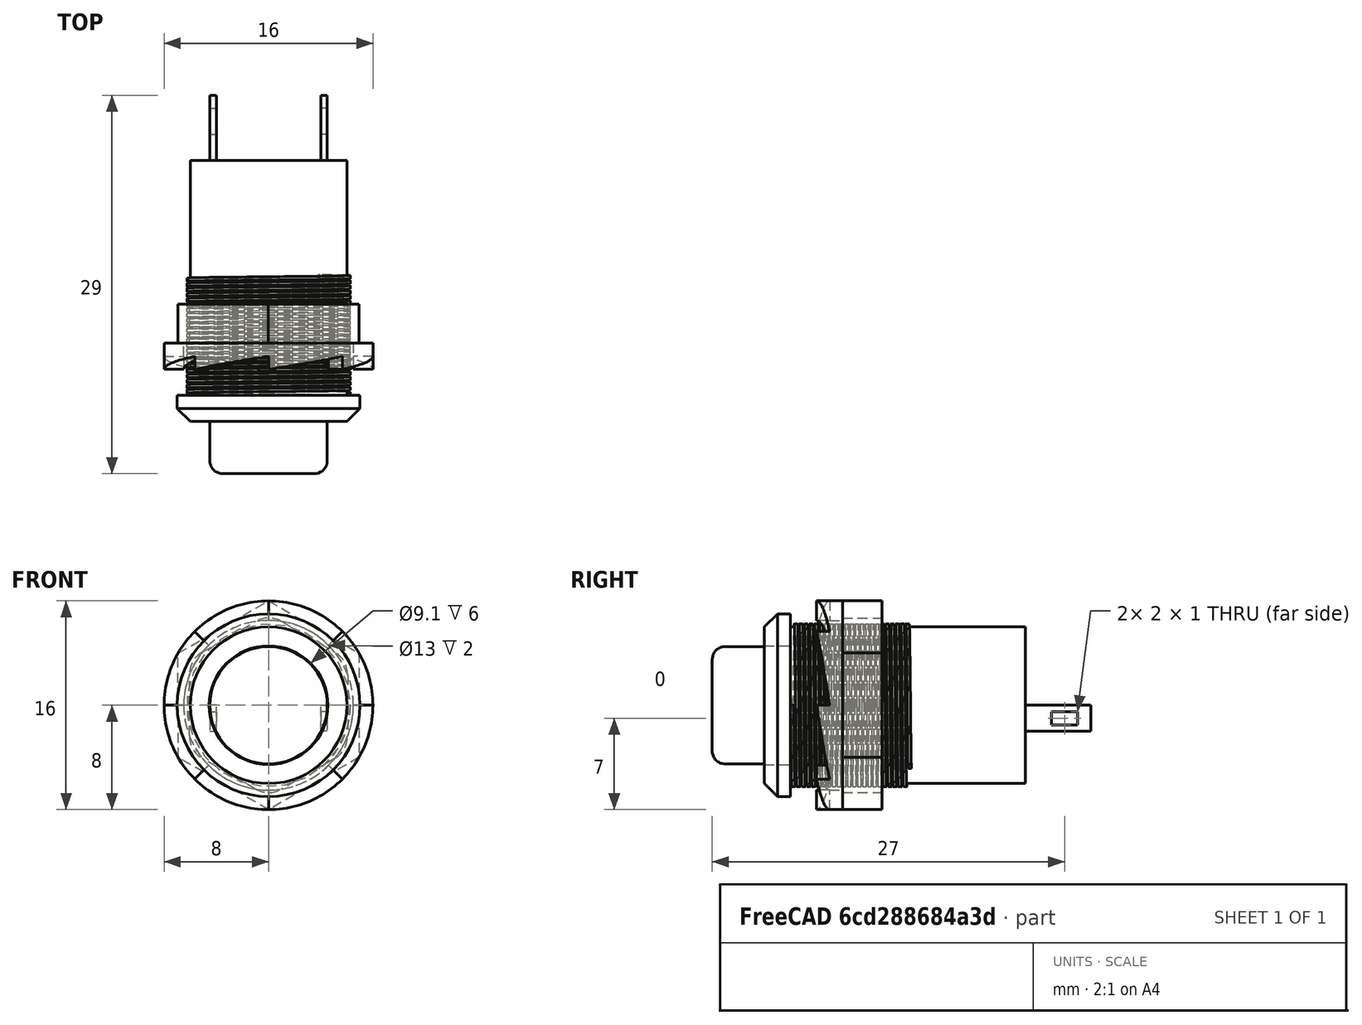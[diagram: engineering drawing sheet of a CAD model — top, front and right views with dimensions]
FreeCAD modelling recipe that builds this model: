
FCSTD DOCUMENT  (FreeCAD 1.1R20260414 (Git shallow))
Label: spring_button
License: All rights reserved
LicenseURL: https://en.wikipedia.org/wiki/All_rights_reserved
objects: Sketcher::SketchObject×9, PartDesign::Pad×6, App::Point×5, PartDesign::Body×4, App::Link×4, App::FeaturePython×4, PartDesign::ShapeBinder×2, PartDesign::Plane×2, PartDesign::Fillet×2, PartDesign::Chamfer×1, PartDesign::Hole×1, PartDesign::AdditiveHelix×1, PartDesign::Pocket×1, PartDesign::Mirrored×1, PartDesign::SubtractiveHelix×1, PartDesign::PolarPattern×1, Assembly::JointGroup×1, Assembly::AssemblyObject×1
note: 69 computed .brp shape members not serialized (recipe doc carries the construction recipe); baked Part::Feature solids carry a one-line shape summary decoded from their .brp

FEATURE [App::Point] Origin001
  Role = Origin
FEATURE [Sketcher::SketchObject] Sketch
  ArcFitTolerance = 1e-06
  AttachmentSupport = -> [Origin]
  ExternalTypes = [0]
  FullyConstrained = true
  MakeInternals = false
  MapMode = 5
  Placement = pos=(0,0,0) rot=(1,0,0;1.5708rad)
  _ExternalGeoVersion = 1
  sketch-geometry (1):
    g0: Circle CenterX=0 CenterY=0 CenterZ=0 NormalX=0 NormalY=0 NormalZ=1 AngleXU=0 Radius=6
  constraints (2):
    c: Diameter(g0) = 12
    c: Coincident(g0,g-1)
FEATURE [PartDesign::Pad] Pad
  Direction = (0,-1,2e-16)
  Length = 18
  Length2 = 10
  Profile = -> Sketch
  ReferenceAxis = -> Sketch [N_Axis]
  Refine = true
  SideType = 0
  Suppressed = false
  Type = 0
  Type2 = 0
FEATURE [Sketcher::SketchObject] Sketch001
  ArcFitTolerance = 1e-06
  AttachmentSupport = -> [Pad]
  ExternalTypes = [0]
  FullyConstrained = true
  MakeInternals = false
  MapMode = 5
  Placement = pos=(0,-18,0) rot=(1,0,0;1.5708rad)
  _ExternalGeoVersion = 1
  sketch-geometry (1):
    g0: Circle CenterX=0 CenterY=0 CenterZ=0 NormalX=0 NormalY=0 NormalZ=1 AngleXU=0 Radius=7
  constraints (2):
    c: Diameter(g0) = 14
    c: Coincident(g0,g-1)
FEATURE [PartDesign::Pad] Pad001
  BaseFeature = -> Pad
  Direction = (0,-1,2e-16)
  Length = 2
  Length2 = 10
  Profile = -> Sketch001
  ReferenceAxis = -> Sketch001 [N_Axis]
  Refine = true
  SideType = 0
  Suppressed = false
  Type = 0
  Type2 = 0
FEATURE [PartDesign::Chamfer] Chamfer
  Angle = 45
  Base = -> Pad001 [Edge6]
  BaseFeature = -> Pad001
  ChamferType = 0
  FlipDirection = false
  Refine = true
  Size = 1
  Size2 = 1
  SupportTransform = false
  Suppressed = false
  UseAllEdges = false
FEATURE [PartDesign::Hole] Hole
  BaseFeature = -> Chamfer
  BaseProfileType = 7
  CustomThreadClearance = 0
  Depth = 6
  DepthType = 0
  Diameter = 9.1
  DrillForDepth = false
  DrillPoint = 0
  DrillPointAngle = 118
  HoleCutCountersinkAngle = 90
  HoleCutCustomValues = false
  HoleCutDepth = 0
  HoleCutDiameter = 0
  HoleCutType = 0
  ModelThread = false
  Profile = -> Chamfer [Face4]
  Refine = true
  Suppressed = false
  Tapered = false
  TaperedAngle = 90
  ThreadClass = 0
  ThreadDepth = 6
  ThreadDepthType = 0
  ThreadDiameter = 9.1
  ThreadDirection = 0
  ThreadFit = 0
  ThreadSize = 0
  ThreadType = 0
  Threaded = false
  UseCustomThreadClearance = false
FEATURE [Sketcher::SketchObject] Sketch004
  ArcFitTolerance = 1e-06
  AttachmentSupport = -> [Origin]
  ExternalTypes = [0]
  FullyConstrained = true
  MakeInternals = false
  MapMode = 5
  _ExternalGeoVersion = 1
  sketch-geometry (4):
    g0: LineSegment StartX=6 StartY=-18 StartZ=0 EndX=6.25 EndY=-18 EndZ=0
    g1: LineSegment StartX=6.25 StartY=-18 StartZ=0 EndX=6.25 EndY=-17.75 EndZ=0
    g2: LineSegment StartX=6.25 StartY=-17.75 StartZ=0 EndX=6 EndY=-17.75 EndZ=0
    g3: LineSegment StartX=6 StartY=-17.75 StartZ=0 EndX=6 EndY=-18 EndZ=0
  constraints (11):
    c: Coincident(g0,g-3)
    c: Horizontal(g0)
    c: Coincident(g1,g0)
    c: Vertical(g1)
    c: Coincident(g2,g1)
    c: PointOnObject(g2,g-3)
    c: Horizontal(g2)
    c: DistanceY(g1,g1) = 0.25
    c: DistanceX(g2,g2) = 0.25
    c: Coincident(g3,g2)
    c: Coincident(g3,g0)
FEATURE [PartDesign::AdditiveHelix] AdditiveHelix
  Angle = 0
  Axis = (0,1,0)
  Base = (0,0,0)
  BaseFeature = -> Hole
  Growth = 0
  HasBeenEdited = true
  Height = 9
  LeftHanded = false
  Mode = 0
  Outside = false
  Pitch = 0.388909
  Profile = -> Sketch004
  ReferenceAxis = -> Sketch004 [V_Axis]
  Refine = true
  Suppressed = false
  Tolerance = 0.1
  Turns = 23.1417
FEATURE [PartDesign::Body] Body  label="base"
  AllowCompound = true
  Group = -> [Sketch,Pad,Sketch001,Pad001,Chamfer,Hole,Sketch004,AdditiveHelix]
  Origin = -> Origin
  Tip = -> AdditiveHelix
FEATURE [App::Point] Origin003
  Role = Origin
FEATURE [PartDesign::ShapeBinder] CopyAdditiveHelix
  TraceSupport = false
FEATURE [PartDesign::Plane] DatumPlane
  AttachmentSupport = -> [CopyAdditiveHelix]
  Length = 60
  MapMode = 5
  Placement = pos=(0,0,0) rot=(0,0.707107,0.707107;3.14159rad)
  ResizeMode = 0
  Width = 60
FEATURE [Sketcher::SketchObject] Sketch005
  ArcFitTolerance = 1e-06
  AttachmentSupport = -> [DatumPlane]
  ExternalGeometry = -> [CopyAdditiveHelix]
  ExternalTypes = [0]
  FullyConstrained = true
  MakeInternals = false
  MapMode = 5
  Placement = pos=(0,0,0) rot=(0,0.707107,0.707107;3.14159rad)
  _ExternalGeoVersion = 1
  sketch-geometry (4):
    g0: LineSegment StartX=4 StartY=0 StartZ=0 EndX=4.5 EndY=0 EndZ=0
    g1: LineSegment StartX=4.5 StartY=0 StartZ=0 EndX=4.5 EndY=-2 EndZ=0
    g2: LineSegment StartX=4.5 StartY=-2 StartZ=0 EndX=4 EndY=-2 EndZ=0
    g3: LineSegment StartX=4 StartY=-2 StartZ=0 EndX=4 EndY=0 EndZ=0
  constraints (12):
    c: Coincident(g0,g1)
    c: Coincident(g1,g2)
    c: Coincident(g2,g3)
    c: Coincident(g3,g0)
    c: Horizontal(g0)
    c: Horizontal(g2)
    c: Vertical(g1)
    c: Vertical(g3)
    c: Distance(g1,g3) = 0.5
    c: Distance(g0,g2) = 2
    c: PointOnObject(g0,g-1)
    c: Distance(g-3,g3) = 2
FEATURE [PartDesign::Pad] Pad002
  Direction = (0,1,-2e-16)
  Length = 5
  Length2 = 10
  Placement = pos=(0,0,0) rot=(0,0.707107,0.707107;3.14159rad)
  Profile = -> Sketch005
  ReferenceAxis = -> Sketch005 [N_Axis]
  Refine = true
  SideType = 0
  Suppressed = false
  Type = 0
  Type2 = 0
FEATURE [Sketcher::SketchObject] Sketch006
  ArcFitTolerance = 1e-06
  AttachmentSupport = -> [Pad002]
  ExternalTypes = [0]
  FullyConstrained = true
  MakeInternals = false
  MapMode = 5
  Placement = pos=(-4.5,-4e-16,4e-16) rot=(0,-1,0;1.5708rad)
  _ExternalGeoVersion = 1
  sketch-geometry (4):
    g0: LineSegment StartX=-1.5 StartY=4 StartZ=0 EndX=-1.5 EndY=2 EndZ=0
    g1: LineSegment StartX=-1.5 StartY=2 StartZ=0 EndX=-0.5 EndY=2 EndZ=0
    g2: LineSegment StartX=-0.5 StartY=2 StartZ=0 EndX=-0.5 EndY=4 EndZ=0
    g3: LineSegment StartX=-0.5 StartY=4 StartZ=0 EndX=-1.5 EndY=4 EndZ=0
  constraints (12):
    c: Coincident(g0,g1)
    c: Coincident(g1,g2)
    c: Coincident(g2,g3)
    c: Coincident(g3,g0)
    c: Vertical(g0)
    c: Vertical(g2)
    c: Horizontal(g1)
    c: Horizontal(g3)
    c: DistanceY(g2,g2) = 2
    c: DistanceX(g3,g3) = 1
    c: Distance(g-2,g2) = 0.5
    c: Distance(g-1,g1) = 2
FEATURE [PartDesign::Pocket] Pocket
  BaseFeature = -> Pad002
  Direction = (1,0,-2e-16)
  Length = 5
  Length2 = 5
  Placement = pos=(0,0,0) rot=(0,0.707107,0.707107;3.14159rad)
  Profile = -> Sketch006
  ReferenceAxis = -> Sketch006 [N_Axis]
  Refine = true
  SideType = 0
  Suppressed = false
  Type = 1
  Type2 = 0
FEATURE [PartDesign::Mirrored] Mirrored
  BaseFeature = -> Pocket
  MirrorPlane = -> YZ_Plane001
  Originals = -> [Pad002,Pocket]
  Placement = pos=(0,0,0) rot=(0,0.707107,0.707107;3.14159rad)
  Refine = true
  Suppressed = false
  TransformMode = 0
FEATURE [PartDesign::Body] Body001  label="pins"
  AllowCompound = true
  Group = -> [DatumPlane,CopyAdditiveHelix,Sketch005,Pad002,Sketch006,Pocket,Mirrored]
  Origin = -> Origin002
  Tip = -> Mirrored
FEATURE [App::Point] Origin005  label="Origin006"
  Role = Origin
FEATURE [PartDesign::ShapeBinder] CopyAdditiveHelix001
  Placement = pos=(0,-20,0) rot=(0,0,1;0rad)
  TraceSupport = false
FEATURE [PartDesign::Plane] DatumPlane001
  AttachmentSupport = -> [CopyAdditiveHelix001]
  Length = 60
  MapMode = 11
  Placement = pos=(0,-20,0) rot=(0.57735,0.57735,-0.57735;2.0944rad)
  ResizeMode = 0
  Width = 60
FEATURE [Sketcher::SketchObject] Sketch007
  ArcFitTolerance = 1e-06
  AttachmentSupport = -> [DatumPlane001]
  ExternalTypes = [0]
  FullyConstrained = true
  MakeInternals = false
  MapMode = 5
  Placement = pos=(0,-20,0) rot=(0.57735,0.57735,-0.57735;2.0944rad)
  _ExternalGeoVersion = 1
  sketch-geometry (1):
    g0: Circle CenterX=0 CenterY=0 CenterZ=0 NormalX=0 NormalY=0 NormalZ=1 AngleXU=0 Radius=4.5
  constraints (2):
    c: Diameter(g0) = 9
    c: Coincident(g0,g-1)
FEATURE [PartDesign::Pad] Pad003
  Direction = (0,-1,0)
  Length = 4
  Length2 = 10
  Placement = pos=(0,-20,0) rot=(0.57735,0.57735,-0.57735;2.0944rad)
  Profile = -> Sketch007
  ReferenceAxis = -> Sketch007 [N_Axis]
  Refine = true
  SideType = 0
  Suppressed = false
  Type = 0
  Type2 = 0
FEATURE [PartDesign::Fillet] Fillet
  Base = -> Pad003 [Edge3]
  BaseFeature = -> Pad003
  Placement = pos=(0,-20,0) rot=(0.57735,0.57735,-0.57735;2.0944rad)
  Radius = 1
  Refine = true
  SupportTransform = false
  Suppressed = false
  UseAllEdges = false
FEATURE [PartDesign::Body] Body002  label="button"
  AllowCompound = true
  Group = -> [DatumPlane001,CopyAdditiveHelix001,Sketch007,Pad003,Fillet]
  Origin = -> Origin004
  Tip = -> Fillet
FEATURE [App::Point] Origin007  label="Origin009"
  Role = Origin
FEATURE [Sketcher::SketchObject] Sketch008
  ArcFitTolerance = 1e-06
  AttachmentSupport = -> [Origin006]
  ExternalTypes = [0]
  FullyConstrained = true
  MakeInternals = false
  MapMode = 5
  Placement = pos=(0,0,0) rot=(1,0,0;1.5708rad)
  _ExternalGeoVersion = 1
  sketch-geometry (2):
    g0: Circle CenterX=0 CenterY=0 CenterZ=0 NormalX=0 NormalY=0 NormalZ=1 AngleXU=0 Radius=8
    g1: Circle CenterX=0 CenterY=0 CenterZ=0 NormalX=0 NormalY=0 NormalZ=1 AngleXU=0 Radius=6.5
  constraints (4):
    c: Diameter(g0) = 16
    c: Coincident(g0,g-1)
    c: Diameter(g1) = 13
    c: Coincident(g1,g0)
FEATURE [PartDesign::Pad] Pad004
  Direction = (0,-1,2e-16)
  Length = 2
  Length2 = 10
  Profile = -> Sketch008
  ReferenceAxis = -> Sketch008 [N_Axis]
  Refine = true
  SideType = 0
  Suppressed = false
  Type = 0
  Type2 = 0
FEATURE [Sketcher::SketchObject] Sketch009
  ArcFitTolerance = 1e-06
  AttachmentSupport = -> [Origin006]
  ExternalGeometry = -> [Pad004]
  ExternalTypes = [0,0]
  FullyConstrained = true
  MakeInternals = false
  MapMode = 5
  _ExternalGeoVersion = 1
  sketch-geometry (4):
    g0: LineSegment StartX=6.5 StartY=-2 StartZ=0 EndX=8 EndY=-2 EndZ=0
    g1: LineSegment StartX=8 StartY=-2 StartZ=0 EndX=8 EndY=-1 EndZ=0
    g2: LineSegment StartX=8 StartY=-1 StartZ=0 EndX=6.5 EndY=-1 EndZ=0
    g3: LineSegment StartX=6.5 StartY=-1 StartZ=0 EndX=6.5 EndY=-2 EndZ=0
  constraints (11):
    c: Coincident(g0,g1)
    c: Coincident(g1,g2)
    c: Coincident(g2,g3)
    c: Coincident(g3,g0)
    c: Horizontal(g0)
    c: Horizontal(g2)
    c: Vertical(g1)
    c: Vertical(g3)
    c: Coincident(g0,g-4)
    c: PointOnObject(g1,g-3)
    c: DistanceY(g1,g1) = 1
FEATURE [PartDesign::SubtractiveHelix] SubtractiveHelix
  Angle = 0
  Axis = (0,1,0)
  Base = (0,0,0)
  BaseFeature = -> Pad004
  Growth = 0
  HasBeenEdited = true
  Height = 1
  LeftHanded = false
  Mode = 0
  Outside = false
  Pitch = 8
  Profile = -> Sketch009
  ReferenceAxis = -> Sketch009 [V_Axis]
  Refine = true
  Reversed = true
  Suppressed = false
  Tolerance = 0.1
  Turns = 0.125
FEATURE [PartDesign::PolarPattern] PolarPattern
  Angle = 360
  Axis = -> Y_Axis003
  BaseFeature = -> SubtractiveHelix
  Mode = 0
  Occurrences = 8
  Offset = 120
  Originals = -> [SubtractiveHelix]
  Refine = true
  SpacingPattern = [0]
  Spacings = [-1,-1,-1,-1,-1,-1,-1]
  Suppressed = false
  TransformMode = 0
FEATURE [Sketcher::SketchObject] Sketch010
  ArcFitTolerance = 1e-06
  AttachmentSupport = -> [PolarPattern]
  ExternalGeometry = -> [PolarPattern]
  ExternalTypes = [0]
  FullyConstrained = false
  MakeInternals = false
  MapMode = 5
  Placement = pos=(0,0,0) rot=(0,0.707107,0.707107;3.14159rad)
  _ExternalGeoVersion = 1
  sketch-geometry (14):
    g0: LineSegment StartX=0.0147037 StartY=7.99999 StartZ=0 EndX=-6.92084 EndY=4.01273 EndZ=0
    g1: LineSegment StartX=-6.92084 StartY=4.01273 StartZ=0 EndX=-6.93554 EndY=-3.98726 EndZ=0
    g2: LineSegment StartX=-6.93554 StartY=-3.98726 StartZ=0 EndX=-0.0147037 EndY=-7.99999 EndZ=0
    g3: LineSegment StartX=-0.0147037 StartY=-7.99999 StartZ=0 EndX=6.92084 EndY=-4.01273 EndZ=0
    g4: LineSegment StartX=6.92084 StartY=-4.01273 StartZ=0 EndX=6.93554 EndY=3.98726 EndZ=0
    g5: LineSegment StartX=6.93554 StartY=3.98726 StartZ=0 EndX=0.0147037 EndY=7.99999 EndZ=0
    g6: Circle [constr] CenterX=0 CenterY=0 CenterZ=0 NormalX=0 NormalY=0 NormalZ=1 AngleXU=0 Radius=8
    g7: LineSegment StartX=0 StartY=6.99999 StartZ=0 EndX=-6.06217 EndY=3.49999 EndZ=0
    g8: LineSegment StartX=-6.06217 StartY=3.49999 StartZ=0 EndX=-6.06217 EndY=-3.49999 EndZ=0
    g9: LineSegment StartX=-6.06217 StartY=-3.49999 StartZ=0 EndX=9e-16 EndY=-6.99999 EndZ=0
    g10: LineSegment StartX=9e-16 StartY=-6.99999 StartZ=0 EndX=6.06217 EndY=-3.49999 EndZ=0
    g11: LineSegment StartX=6.06217 StartY=-3.49999 StartZ=0 EndX=6.06217 EndY=3.49999 EndZ=0
    g12: LineSegment StartX=6.06217 StartY=3.49999 StartZ=0 EndX=0 EndY=6.99999 EndZ=0
    g13: Circle [constr] CenterX=0 CenterY=0 CenterZ=0 NormalX=0 NormalY=0 NormalZ=1 AngleXU=0 Radius=6.99999
  constraints (31):
    c: Coincident(g0,g1)
    c: Coincident(g1,g2)
    c: Coincident(g2,g3)
    c: Coincident(g3,g4)
    c: Coincident(g4,g5)
    c: Coincident(g5,g0)
    c: Equal(g0, g1-g5) x5
    c: PointOnObject(g0,g6)
    c: PointOnObject(g1,g6)
    c: PointOnObject(g2,g6)
    c: PointOnObject(g3,g6)
    c: PointOnObject(g4,g6)
    c: PointOnObject(g5,g6)
    c: Coincident(g6,g-3)
    c: PointOnObject(g5,g-3)
    c: Coincident(g7,g8)
    c: Coincident(g8,g9)
    c: Coincident(g9,g10)
    c: Coincident(g10,g11)
    c: Coincident(g11,g12)
    c: Coincident(g12,g7)
    c: Equal(g7, g8-g12) x5
    c: PointOnObject(g7,g13)
    c: PointOnObject(g8,g13)
    c: PointOnObject(g9,g13)
    c: PointOnObject(g10,g13)
    c: PointOnObject(g11,g13)
    c: PointOnObject(g12,g13)
    c: Coincident(g13,g6)
    c: PointOnObject(g12,g-2)
    c: DistanceY(g7,g0) = 1
FEATURE [PartDesign::Pad] Pad005
  BaseFeature = -> PolarPattern
  Direction = (0,1,-2e-16)
  Length = 3
  Length2 = 10
  Profile = -> Sketch010
  ReferenceAxis = -> Sketch010 [N_Axis]
  Refine = true
  SideType = 0
  Suppressed = false
  Type = 0
  Type2 = 0
FEATURE [PartDesign::Fillet] Fillet001
  Base = -> Pad005 [Edge113,Edge118,Edge117,Edge114,Edge116,Edge115]
  BaseFeature = -> Pad005
  Radius = 2
  Refine = true
  SupportTransform = false
  Suppressed = false
  UseAllEdges = false
FEATURE [PartDesign::Body] Body003  label="nut"
  AllowCompound = true
  Group = -> [Sketch008,Pad004,Sketch009,SubtractiveHelix,PolarPattern,Sketch010,Pad005,Fillet001]
  Origin = -> Origin006
  Placement = pos=(0,-14,0) rot=(0,0,1;0rad)
  Tip = -> Fillet001
FEATURE [App::Point] Origin009  label="Origin011"
  Role = Origin
FEATURE [App::Link] base  label="base001"
  LinkedObject = -> Body
FEATURE [App::FeaturePython] GroundedJoint  # Assembly grounded joint (typed FeaturePython)
  ObjectToGround = -> base
FEATURE [App::Link] pins  label="pins001"
  LinkPlacement = pos=(-0.25,7e-16,1) rot=(0,0,1;0rad)
  LinkedObject = -> Body001
  Placement = pos=(-0.25,7e-16,1) rot=(0,0,1;0rad)
FEATURE [App::Link] nut  label="nut001"
  LinkPlacement = pos=(0,-11.7053,2.6e-15) rot=(0,0,1;0rad)
  LinkedObject = -> Body003
  Placement = pos=(0,-11.7053,2.6e-15) rot=(0,0,1;0rad)
FEATURE [App::Link] button  label="button001"
  LinkPlacement = pos=(-4.8e-15,1.5,-4.6e-15) rot=(0,1,0;1.5708rad)
  LinkedObject = -> Body002
  Placement = pos=(-4.8e-15,1.5,-4.6e-15) rot=(0,1,0;1.5708rad)
FEATURE [App::FeaturePython] Joint  label="Slider004"  # Assembly joint (typed FeaturePython)
  Angle = 0
  AngleMax = 0
  AngleMin = 0
  Detach1 = false
  Detach2 = false
  Distance = 0
  Distance2 = 0
  EnableAngleMax = false
  EnableAngleMin = false
  EnableLengthMax = false
  EnableLengthMin = false
  JointType = 3 (Slider)
  LengthMax = 0
  LengthMin = 0
  Placement1 = pos=(2e-16,-21.5,0) rot=(0.57735,0.57735,-0.57735;2.0944rad)
  Placement2 = pos=(0,-20,0) rot=(0,-0.707107,0.707107;3.14159rad)
  Reference1 = -> button [Face1,Face1]
  Reference2 = -> base [Edge50,Edge50]
  Suppressed = false
FEATURE [App::FeaturePython] Joint001  label="Fixed"  # Assembly joint (typed FeaturePython)
  Angle = 0
  AngleMax = 0
  AngleMin = 0
  Detach1 = false
  Detach2 = false
  Distance = 0
  Distance2 = 0
  EnableAngleMax = false
  EnableAngleMin = false
  EnableLengthMax = false
  EnableLengthMin = false
  JointType = 0 (Fixed)
  LengthMax = 0
  LengthMin = 0
  Offset1 = pos=(0,4,0) rot=(0,0,1;0rad)
  Placement1 = pos=(0.25,-2e-16,-1) rot=(-0.57735,0.57735,-0.57735;4.18879rad)
  Placement2 = pos=(0,0,1e-16) rot=(0.57735,0.57735,0.57735;4.18879rad)
  Reference1 = -> pins [Face14,Face14]
  Reference2 = -> base [Face105,Face105]
  Suppressed = false
FEATURE [App::FeaturePython] Joint002  label="Revolute004"  # Assembly joint (typed FeaturePython)
  Angle = 0
  AngleMax = 0
  AngleMin = 0
  Detach1 = false
  Detach2 = false
  Distance = 0
  Distance2 = 0
  EnableAngleMax = false
  EnableAngleMin = false
  EnableLengthMax = false
  EnableLengthMin = false
  JointType = 1 (Revolute)
  LengthMax = 0
  LengthMin = 0
  Offset2 = pos=(0,0,8) rot=(0,0,1;0rad)
  Placement1 = pos=(0,-0.777778,2e-16) rot=(1,0,0;1.5708rad)
  Placement2 = pos=(0,-12.4831,2.8e-15) rot=(1,0,0;1.5708rad)
  Reference1 = -> nut [Fillet001.Face38,Fillet001.Face38]
  Reference2 = -> base [AdditiveHelix.Face101,AdditiveHelix.Face101]
  Suppressed = false
FEATURE [Assembly::JointGroup] Joints
  Group = -> [GroundedJoint,Joint,Joint001,Joint002]
FEATURE [Assembly::AssemblyObject] Assembly
  Group = -> [Joints,base,GroundedJoint,pins,nut,button,Joint,Joint001,Joint002]
  Origin = -> Origin008
  Type = Assembly
